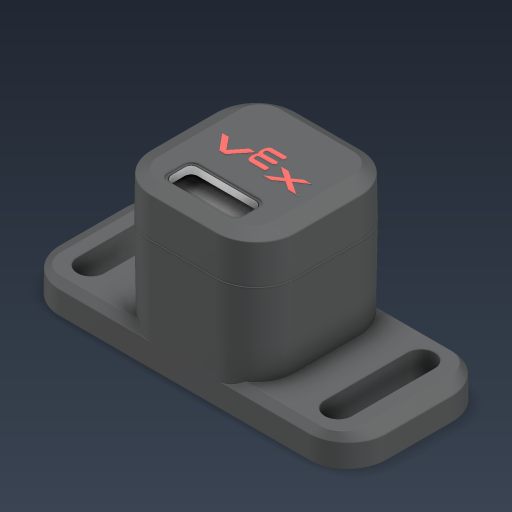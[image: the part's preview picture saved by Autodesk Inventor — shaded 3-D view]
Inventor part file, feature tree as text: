
AUTODESK INVENTOR PART (.ipt)
format: ipt  version: 2023 (Build 270158000, 158)  size: 2,642,432 bytes
history: native  units: in
note: dims shown in document units (in); Inventor stores cm internally (conversion verified against a paired STEP export)
features: other x12, extrude x3, sketch x3
ambient origin geometry x8: Origin, YZ Plane, XZ Plane, XY Plane, X Axis, Y Axis, Z Axis, Center Point
bodies: Solid1 (feature_tree), Solid2 (feature_tree), Solid3 (feature_tree), Solid4 (feature_tree), Solid5 (feature_tree), Solid6 (feature_tree), Solid7 (feature_tree), Solid8 (feature_tree), Solid9 (feature_tree), Solid10 (feature_tree)
feature tree (18):
  other  "V5 Optical Sensor.iam"
  other  "276-7043-003 Web.ipt:1"
  other  "276-7043-002 Web.ipt:1"
  other  "276-7043-006 Web.ipt:1"
  other  "276-7043-001 Web_Dual Flange.ipt:1"
  other  "228-2677-006 Web.ipt:1"
  other  "228-2677-006 Web.ipt:2"
  other  "228-2677-006 Web.ipt:3"
  other  "228-2677-006 Web.ipt:4"
  other  "276-7043-900 Web.iam:1::Part40^276-7043-900 Web.ipt:1"
  extrude  "Extrusion1"  Depth=0.3937in
  sketch  "Sketch1"  dims[d0=0.3937in d1=0.089in]
  other  "Srf1"
  sketch  "Sketch2"  dims[d2=1.0in d3=0.0in d4=0.089in]
  other  "Srf2"
  sketch  "Sketch3"  dims[d5=1.0in d6=0.0in d11=0.002in d12=0.0in]
  extrude  "ExtrusionSrf1"  Depth=0.089in
  extrude  "ExtrusionSrf2"  Depth=0.002in TaperAngle=0.0deg
